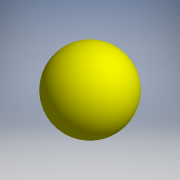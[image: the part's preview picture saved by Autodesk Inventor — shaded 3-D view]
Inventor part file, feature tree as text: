
AUTODESK INVENTOR PART (.ipt)
format: ipt  version: 2017.3 (Build 213256000, 256)  size: 113,152 bytes
history: native  units: mm (DEFAULTED — no unit token found)
features: other x7, revolve x1, sketch x1
ambient origin geometry x8: Origin, YZ Plane, XZ Plane, XY Plane, X Axis, Y Axis, Z Axis, Center Point
bodies: Solid1 (feature_tree)
feature tree (9):
  revolve  "Revolution1"  [1 undecoded]
  other  "ball_XY"
  other  "ball_YZ"
  other  "ball_ZX"
  other  "ball_X"
  other  "ball_Y"
  other  "ball_Z"
  other  "ball_Center"
  sketch  "Sketch_1"  dims[d0=360.0deg]
note: 1 required parameter value undecoded (feature->parameter linkage not recoverable at this tier; creation-order binding heuristic only, values carry confidence <= 0.55)
